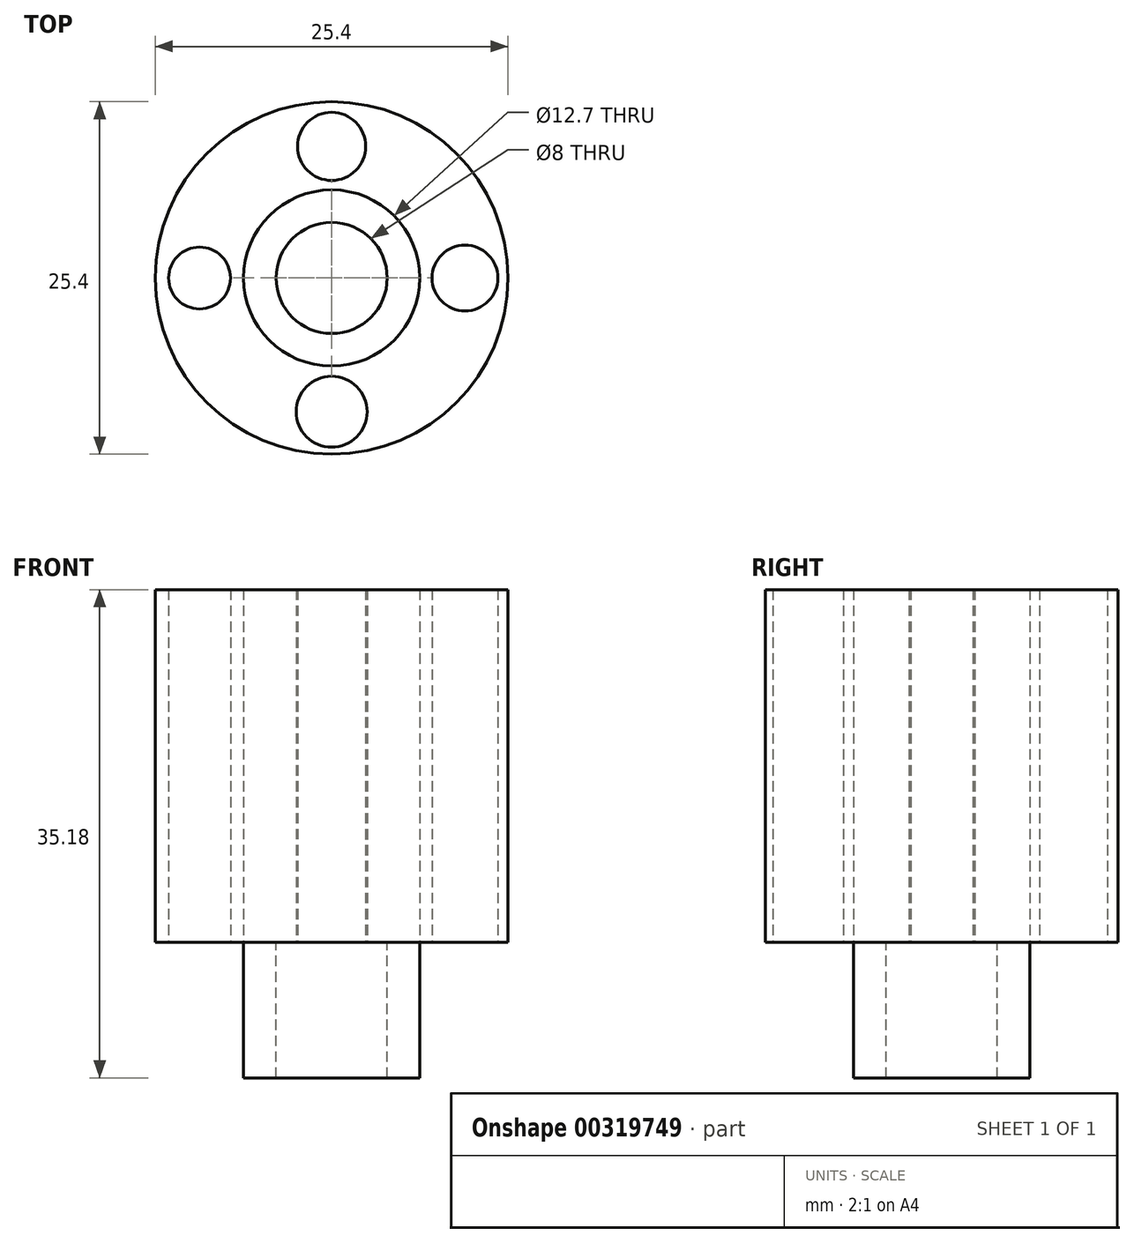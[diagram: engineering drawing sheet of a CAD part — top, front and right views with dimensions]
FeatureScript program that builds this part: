
annotation { "Feature Type Name" : "Feature", "Feature Type Description" : "" }
export const myFeature = defineFeature(function(context is Context, id is Id, definition is map)
    precondition{}
    {
        {
            var Q0;
            Q0=qCreatedBy(makeId("Top.planeOp"),FACE);
            var sketch = newSketch(context, id + "F0", { "sketchPlane" : qUnion([Q0])});
            skCircle(sketch, "E0", {"center": v(0, 0) * mm, "radius": 6.35 * mm});
            skCircle(sketch, "E1", {"center": v(0, 0) * mm, "radius": 4 * mm});
            skCircle(sketch, "E2", {"center": v(0, 0) * mm, "radius": 12.7 * mm});
            skCircle(sketch, "E3", {"center": v(-0.29, 0) * mm, "radius": 0.04 * mm});
            skCircle(sketch, "E4", {"center": v(0, 0.3) * mm, "radius": 0.04 * mm});
            skCircle(sketch, "E5", {"center": v(0.29, 0) * mm, "radius": 0.04 * mm});
            skCircle(sketch, "E6", {"center": v(0, -0.29) * mm, "radius": 0.04 * mm});
            skCircle(sketch, "E7", {"center": v(-9.51, 0) * mm, "radius": 2.23 * mm});
            skCircle(sketch, "E8", {"center": v(0, 9.49) * mm, "radius": 2.46 * mm});
            skCircle(sketch, "E9", {"center": v(9.6, 0) * mm, "radius": 2.37 * mm});
            skCircle(sketch, "E10", {"center": v(0, -9.63) * mm, "radius": 2.55 * mm});
            skSolve(sketch);
        }
        {
            var Q0;
            Q0=makeQuery(id+"F0.imprint","IMPRINT",FACE,{"disambiguationData":[TD([[makeQuery(id+"F0.imprint","IMPRINT",EDGE,{"derivedFrom":sQuery(id+"F0.wireOp",EDGE,"E0")}),1.0]])]});
            extrude(context, id + "F1", {"entities" : qUnion([Q0]), "oppositeDirection" : true, "depth" : 9.78 * mm});
        }
        {
            var Q0;
            Q0 = qSketchRegion(id + "F0", true);
            extrude(context, id + "F2", {"entities" : qUnion([Q0]), "operationType" : NewBodyOperationType.ADD, "depth" : 25.4 * mm});
        }
    });
